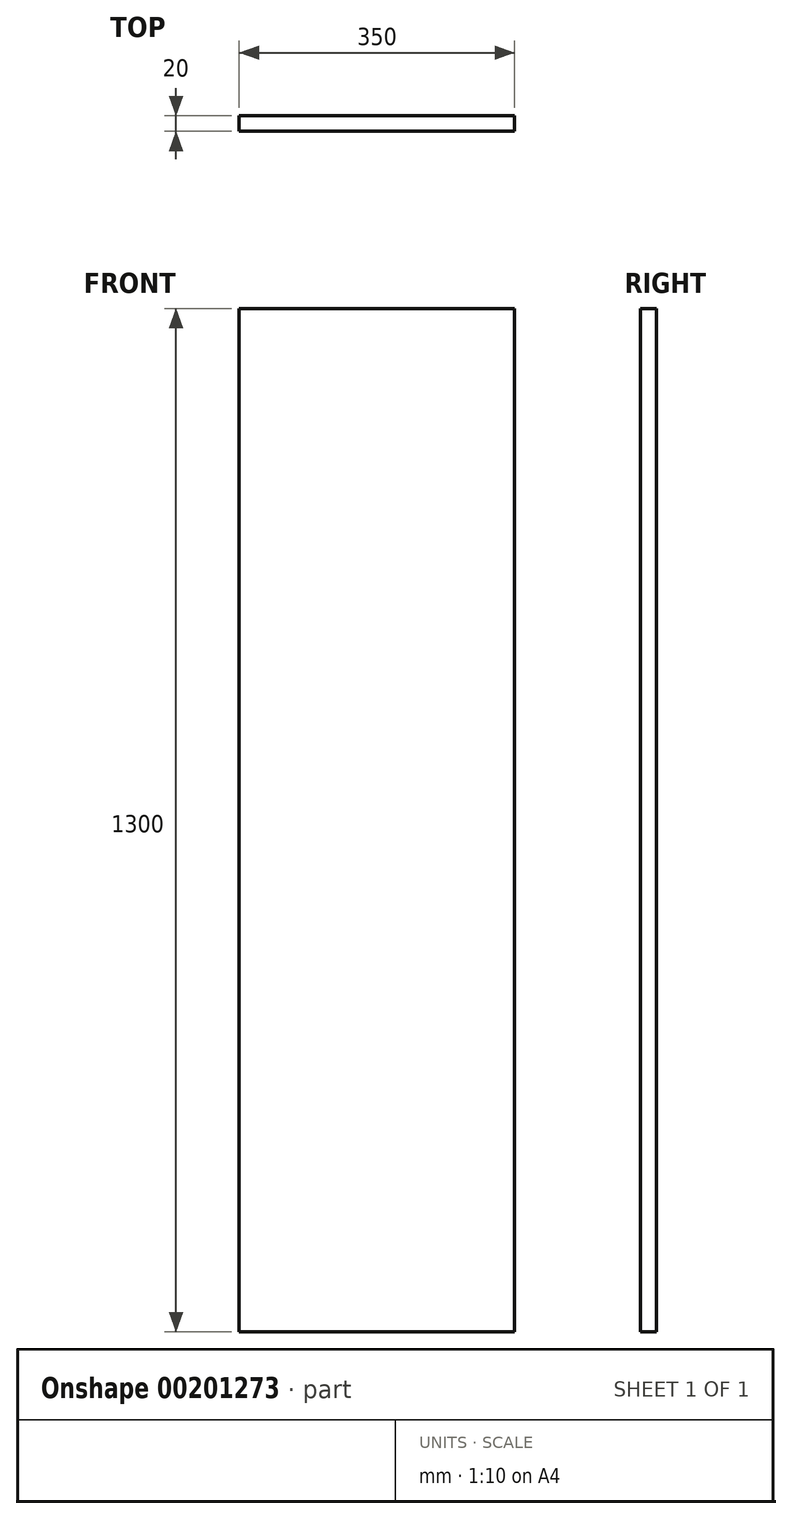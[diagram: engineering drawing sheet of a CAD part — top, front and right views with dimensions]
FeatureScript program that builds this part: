
annotation { "Feature Type Name" : "Feature", "Feature Type Description" : "" }
export const myFeature = defineFeature(function(context is Context, id is Id, definition is map)
    precondition{}
    {
        {
            var Q0;
            Q0=qCreatedBy(makeId("Top.planeOp"),FACE);
            var sketch = newSketch(context, id + "F0", { "sketchPlane" : qUnion([Q0])});
            skLineSegment(sketch, "E0.bottom", {"start": v(0, 0) * mm, "end": v(350, 0) * mm});
            skLineSegment(sketch, "E0.top", {"start": v(0, 20) * mm, "end": v(350, 20) * mm});
            skLineSegment(sketch, "E0.left", {"start": v(0, 0) * mm, "end": v(0, 20) * mm});
            skLineSegment(sketch, "E0.right", {"start": v(350, 0) * mm, "end": v(350, 20) * mm});
            skSolve(sketch);
        }
        {
            var Q0;
            Q0=qSketchRegion(id+"F0",true);
            extrude(context, id + "F1", {"entities" : qUnion([Q0]), "depth" : 1300 * mm});
        }
    });
